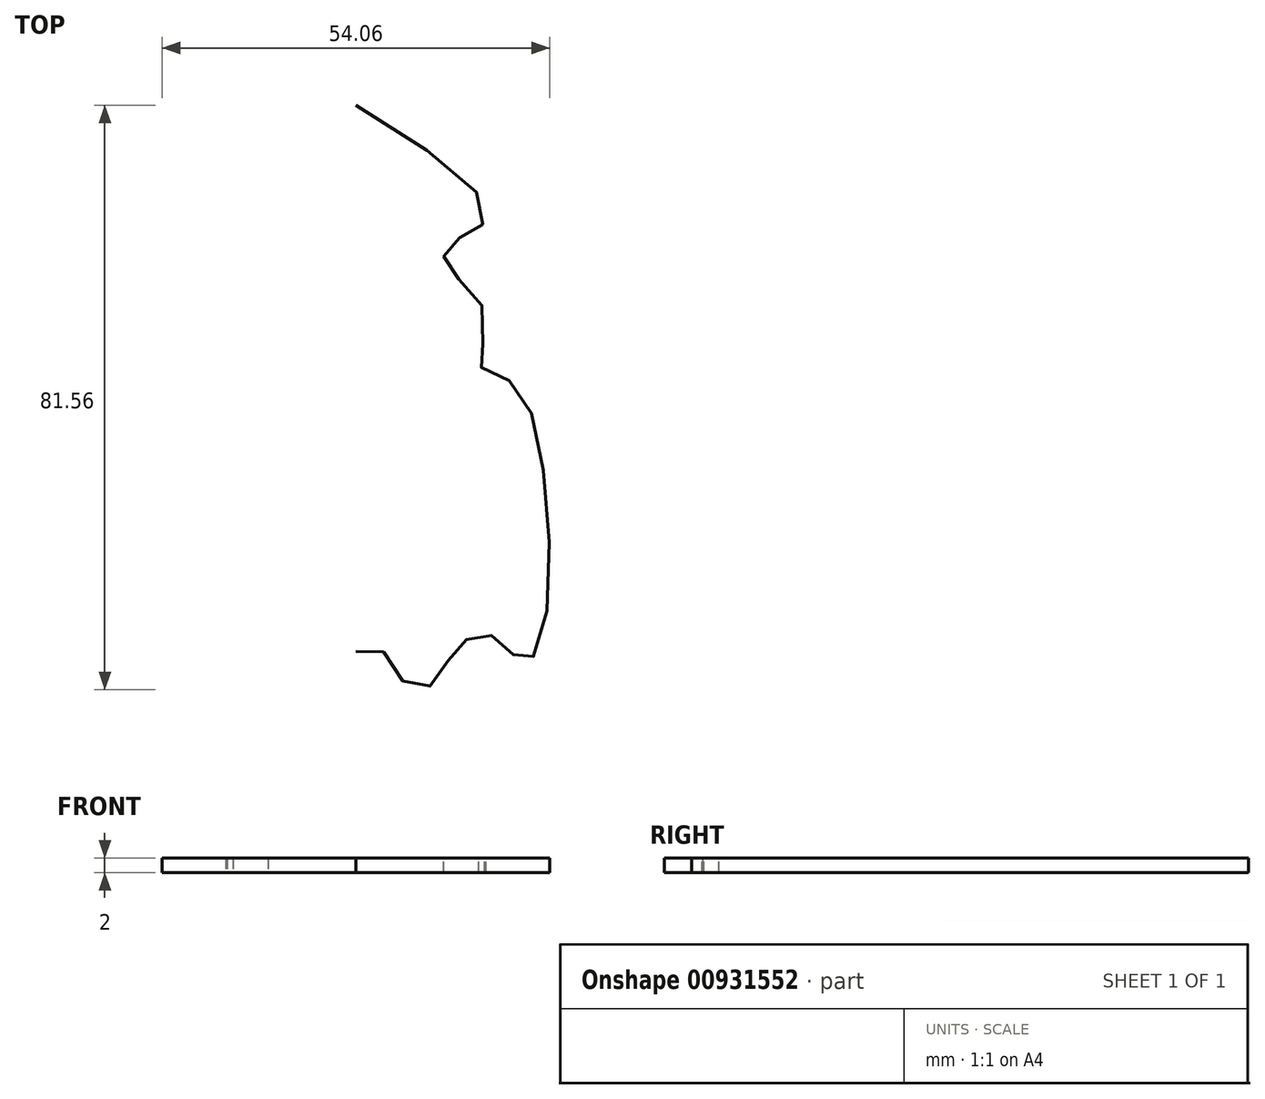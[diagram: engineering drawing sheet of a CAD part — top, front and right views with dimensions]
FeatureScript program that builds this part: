
annotation { "Feature Type Name" : "Feature", "Feature Type Description" : "" }
export const myFeature = defineFeature(function(context is Context, id is Id, definition is map)
    precondition{}
    {
        {
            var Q0;
            Q0=qCreatedBy(makeId("Top.planeOp"),FACE);
            var sketch = newSketch(context, id + "F0", { "sketchPlane" : qUnion([Q0])});
            skFitSpline(sketch, "E0", {"points": [v(0, 37.65) * mm, v(-18.14, 23.08) * mm, v(-16.15, 19.7) * mm, v(-13.24, 18.53) * mm, v(-12.49, 15.07) * mm, v(-16.7, 11.52) * mm, v(-17.73, 4.4) * mm, v(-17.35, 1.23) * mm, v(-21.57, -0.9) * mm, v(-25.77, -10.85) * mm, v(-26.3, -35.17) * mm, v(-23.37, -40.09) * mm, v(-20.08, -36.93) * mm, v(-17.32, -36.34) * mm, v(-13.81, -38.03) * mm, v(-11.6, -42.32) * mm, v(-7.57, -43.62) * mm, v(-3.93, -38.68) * mm, v(0, -38.55) * mm], "startDerivative": vector(-234.79, -144.9) * mm, "endDerivative": vector(129.23, 17.1) * mm});
            skLineSegment(sketch, "E1", {"start": v(0, 37.65) * mm, "end": v(0, -38.55) * mm, "construction": true});
            skFitSpline(sketch, "E2.MirrorCS", {"points": [v(0, 37.65) * mm, v(18.14, 23.08) * mm, v(16.15, 19.7) * mm, v(13.24, 18.53) * mm, v(12.49, 15.07) * mm, v(16.7, 11.52) * mm, v(17.73, 4.4) * mm, v(17.35, 1.23) * mm, v(21.57, -0.9) * mm, v(25.77, -10.85) * mm, v(26.3, -35.17) * mm, v(23.37, -40.09) * mm, v(20.08, -36.93) * mm, v(17.32, -36.34) * mm, v(13.81, -38.03) * mm, v(11.6, -42.32) * mm, v(7.57, -43.62) * mm, v(3.93, -38.68) * mm, v(0, -38.55) * mm], "startDerivative": vector(234.79, -144.9) * mm, "endDerivative": vector(-129.23, 17.1) * mm});
            skSolve(sketch);
        }
        {
            var Q0;
            Q0=makeQuery(id+"F0.imprint","IMPRINT",FACE,{"disambiguationData":[TD([[makeQuery(id+"F0.imprint","IMPRINT",EDGE,{"derivedFrom":sQuery(id+"F0.wireOp",EDGE,"E0")}),1.0]])]});
            extrude(context, id + "F1", {"entities" : qUnion([Q0]), "depth" : 2 * mm, "offsetDistance" : 25 * mm});
        }
    });
